# Revit family: Heater-BERKO-Explosion_Proof_Convector
name_source: partatom
category: Mechanical Equipment
units: mm (PartAtom-declared; Revit-internal decimal feet)

## family parameters
Classification = None
Cut with Voids When Loaded = No
Host = Face
OmniClass Number = 23.75.70.17.14
OmniClass Title = Convectors
Part Type = Normal
Room Calculation Point = No
Round Connector Dimension = Use Diameter
Shared = No

## types (4) — shared parameters
Default Elevation = 3' - 0"
Description = Electric explosion proof convection heater
Frequency = 60 Hz
Instruction Sheet Link = https://www.marleymep.com
Manufacturer = Marley® Engineered Products
Material = Paint - Beige
Number of Poles = 1
Power Factor = 1
Product Documentation Link = https://www.marleymep.com
Product Name = Explosion - Proof Convection Heater Gen2
Product Page URL = https://www.marleymep.com
URL = https://www.marleymep.com
Version = 2020 - v1.0a

## per-type parameters (varying)
| type | Amps | Classification | Controls Only | Depth | Height | Length | Phase | S1 - L 26in | S2 - L 26in | S2 - L 39in | S2 - L 67.5in | Shipping Weight | Thermostat only or w/controls | Total Heating Capacity | Unit Size | Voltage | Watts |
| BX-254-F0310052B | 4 A | Class I- Divisions 1 & 2- Groups B- C & D / Class I- Zones 1 & 2 Groups IIB + H2 / Ignition Temperature Code T2A- 536° F |  | 0' - 4 1/2" | 0' - 6" | 2' - 2" | 1 | Yes | No | No | No | 13 lbs | 1024754 | 1706.0 Btu/h | 1 | 120 V | 500 W |
| BX-254-F0330362C | 17 A | Class I- Divisions 1 & 2- Groups B- C & D / Class I- Zones 1 & 2 Groups IIB + H2 / Ignition Temperature Code T2A- 536° F | Not Required | 0' - 8" | 1' - 4" | 3' - 3" | 1 | No | No | Yes | No | 36 lbs | S2 | 12283.0 Btu/h | 3 | 208 V | 3600 W |
| BX-254-F0320183U | 2 A | Class I- Divisions 1 & 2- Groups C & D / Class I- Zones 1 & 2 Groups IIB / Ignition Temperature Code T2A- 536° F | B2 | 0' - 8" | 1' - 4" | 2' - 2" | 3 | No | Yes | No | No | 27 lbs | B2S1 | 6140.0 Btu/h | 2 | 480 V | 1800 W |
| BX-254-F0840324Z | 3 A | Class I- Divisions 1 & 2- Groups B- C & D / Class II- Divisions 1 & 2- Groups E- F & G / Ignition Temperature Code T3C- 320° F | B2 | 0' - 8" | 1' - 4" | 5' - 7 1/2" | 3 | No | No | No | Yes | 60 lbs | B2S1 | 10918.0 Btu/h | 4 | 600 V | 3200 W |

note: column(s) folded — value = type name in every type: Model

## geometry (parser evidence)
native form markers: Sweep x19
no freeform markers — native parametric forms only
